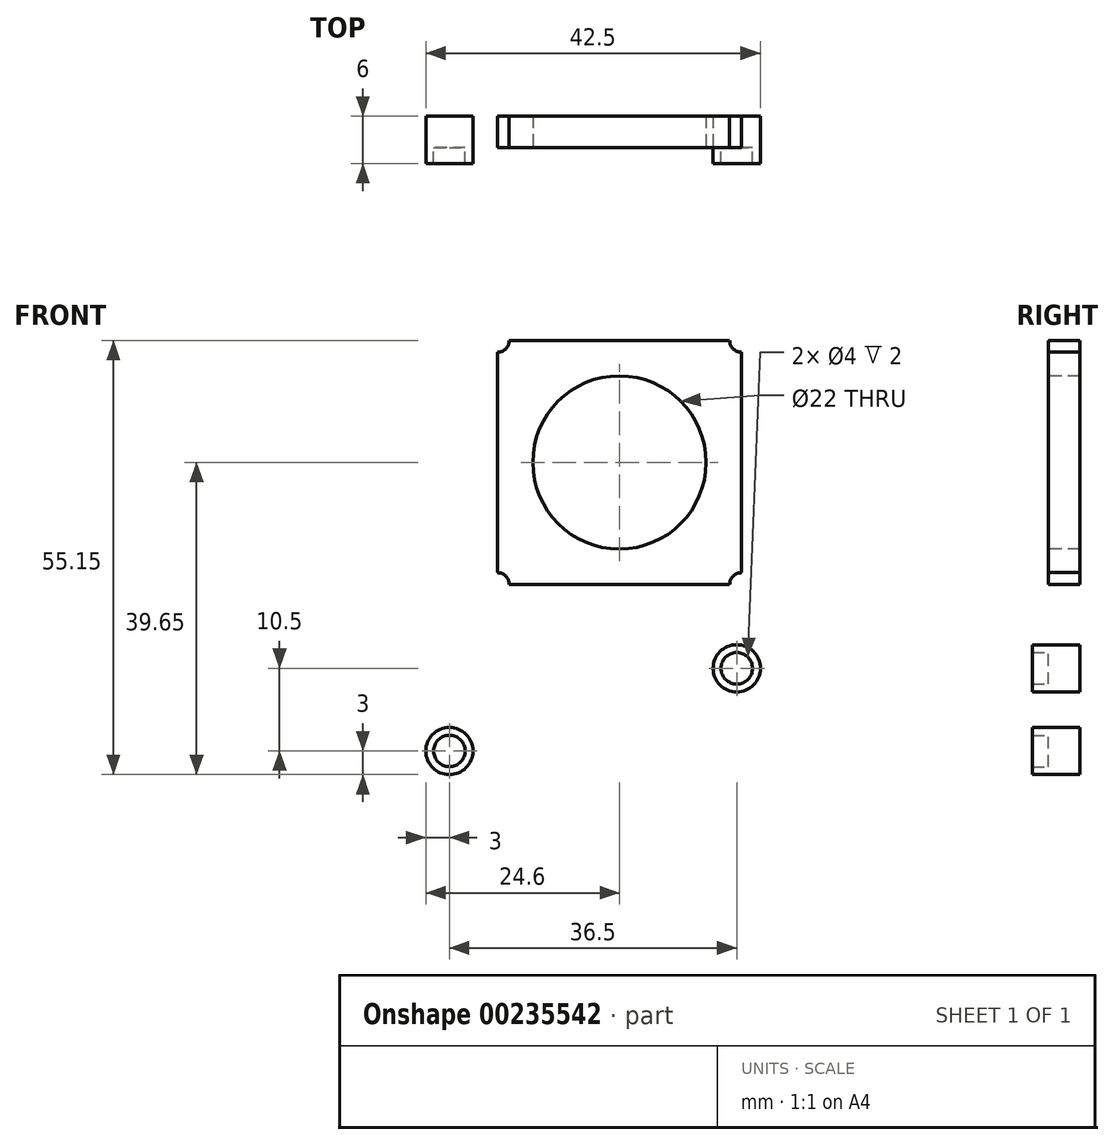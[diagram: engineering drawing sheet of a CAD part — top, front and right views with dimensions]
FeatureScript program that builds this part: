
annotation { "Feature Type Name" : "Feature", "Feature Type Description" : "" }
export const myFeature = defineFeature(function(context is Context, id is Id, definition is map)
    precondition{}
    {
        {
            var Q0;
            Q0=qCreatedBy(makeId("Front.planeOp"),FACE);
            var sketch = newSketch(context, id + "F0", { "sketchPlane" : qUnion([Q0])});
            skLineSegment(sketch, "E0.bottom", {"start": v(21.15, -21.15) * mm, "end": v(-21.15, -21.15) * mm});
            skLineSegment(sketch, "E0.top", {"start": v(21.15, 21.15) * mm, "end": v(-21.15, 21.15) * mm});
            skLineSegment(sketch, "E0.left", {"start": v(21.15, -21.15) * mm, "end": v(21.15, 21.15) * mm});
            skLineSegment(sketch, "E0.right", {"start": v(-21.15, -21.15) * mm, "end": v(-21.15, 21.15) * mm});
            skPoint(sketch, "E0.middle", {"position": v(0, 0) * mm});
            skLineSegment(sketch, "E1.bottom", {"start": v(15.5, -15.5) * mm, "end": v(-15.5, -15.5) * mm});
            skLineSegment(sketch, "E1.top", {"start": v(15.5, 15.5) * mm, "end": v(-15.5, 15.5) * mm});
            skLineSegment(sketch, "E1.left", {"start": v(15.5, -15.5) * mm, "end": v(15.5, 15.5) * mm});
            skLineSegment(sketch, "E1.right", {"start": v(-15.5, -15.5) * mm, "end": v(-15.5, 15.5) * mm});
            skCircle(sketch, "E2", {"center": v(-15.5, 15.5) * mm, "radius": 1.5 * mm});
            skCircle(sketch, "E3", {"center": v(15.5, 15.5) * mm, "radius": 1.5 * mm});
            skCircle(sketch, "E4", {"center": v(-15.5, -15.5) * mm, "radius": 1.5 * mm});
            skCircle(sketch, "E5", {"center": v(15.5, -15.5) * mm, "radius": 1.5 * mm});
            skLineSegment(sketch, "E6.bottom", {"start": v(-21.15, -21.15) * mm, "end": v(21.15, -21.15) * mm});
            skLineSegment(sketch, "E6.top", {"start": v(-21.15, -46.15) * mm, "end": v(21.15, -46.15) * mm});
            skLineSegment(sketch, "E6.right", {"start": v(21.15, -21.15) * mm, "end": v(21.15, -46.15) * mm});
            skCircle(sketch, "E7", {"center": v(0, 0) * mm, "radius": 11 * mm});
            skLineSegment(sketch, "E8.bottom", {"start": v(-21.15, 21.15) * mm, "end": v(21.15, 21.15) * mm});
            skLineSegment(sketch, "E8.top", {"start": v(-21.15, 26.15) * mm, "end": v(21.15, 26.15) * mm});
            skLineSegment(sketch, "E8.left", {"start": v(-21.15, 21.15) * mm, "end": v(-21.15, 26.15) * mm});
            skLineSegment(sketch, "E8.right", {"start": v(21.15, 21.15) * mm, "end": v(21.15, 26.15) * mm});
            skLineSegment(sketch, "E9.bottom", {"start": v(21.15, 26.15) * mm, "end": v(26.15, 26.15) * mm});
            skLineSegment(sketch, "E9.top", {"start": v(21.15, -46.15) * mm, "end": v(26.15, -46.15) * mm});
            skLineSegment(sketch, "E9.left", {"start": v(21.15, 26.15) * mm, "end": v(21.15, -46.15) * mm});
            skLineSegment(sketch, "E9.right", {"start": v(26.15, 26.15) * mm, "end": v(26.15, -46.15) * mm});
            skLineSegment(sketch, "E10.bottom", {"start": v(-21.15, 26.15) * mm, "end": v(-26.15, 26.15) * mm});
            skLineSegment(sketch, "E10.top", {"start": v(-21.15, -46.15) * mm, "end": v(-26.15, -46.15) * mm});
            skLineSegment(sketch, "E10.left", {"start": v(-21.15, 26.15) * mm, "end": v(-21.15, -21.15) * mm});
            skLineSegment(sketch, "E10.right", {"start": v(-26.15, 26.15) * mm, "end": v(-26.15, -46.15) * mm});
            skLineSegment(sketch, "E11.right", {"start": v(-26.15, -41.15) * mm, "end": v(-26.15, -46.15) * mm});
            skLineSegment(sketch, "E12.bottom", {"start": v(-26.15, 26.15) * mm, "end": v(-21.15, 26.15) * mm});
            skLineSegment(sketch, "E12.top", {"start": v(-26.15, 21.15) * mm, "end": v(-21.15, 21.15) * mm});
            skLineSegment(sketch, "E12.left", {"start": v(-26.15, 26.15) * mm, "end": v(-26.15, 21.15) * mm});
            skLineSegment(sketch, "E12.right", {"start": v(-21.15, 26.15) * mm, "end": v(-21.15, 21.15) * mm});
            skLineSegment(sketch, "E13.bottom", {"start": v(26.15, 26.15) * mm, "end": v(21.15, 26.15) * mm});
            skLineSegment(sketch, "E13.top", {"start": v(26.15, 21.15) * mm, "end": v(21.15, 21.15) * mm});
            skLineSegment(sketch, "E13.left", {"start": v(26.15, 26.15) * mm, "end": v(26.15, 21.15) * mm});
            skLineSegment(sketch, "E13.right", {"start": v(21.15, 26.15) * mm, "end": v(21.15, 21.15) * mm});
            skLineSegment(sketch, "E14.bottom", {"start": v(21.15, -21.15) * mm, "end": v(26.15, -21.15) * mm});
            skLineSegment(sketch, "E14.right", {"start": v(26.15, -21.15) * mm, "end": v(26.15, -46.15) * mm});
            skLineSegment(sketch, "E15.bottom", {"start": v(21.15, 26.15) * mm, "end": v(5.15, 26.15) * mm});
            skLineSegment(sketch, "E15.top", {"start": v(21.15, 21.15) * mm, "end": v(5.15, 21.15) * mm});
            skLineSegment(sketch, "E15.right", {"start": v(5.15, 26.15) * mm, "end": v(5.15, 21.15) * mm});
            skLineSegment(sketch, "E16", {"start": v(-21.15, -21.15) * mm, "end": v(-26.15, -21.15) * mm});
            skLineSegment(sketch, "E17", {"start": v(-26.15, -21.15) * mm, "end": v(-21.15, 21.15) * mm});
            skLineSegment(sketch, "E18", {"start": v(15.5, -15.5) * mm, "end": v(14, -15.5) * mm});
            skLineSegment(sketch, "E19", {"start": v(14.9, -13.34) * mm, "end": v(14.9, -14.84) * mm});
            skLineSegment(sketch, "E20", {"start": v(14.9, -14.84) * mm, "end": v(14.9, -26.15) * mm});
            skCircle(sketch, "E21", {"center": v(14.9, -26.15) * mm, "radius": 2 * mm});
            skCircle(sketch, "E22", {"center": v(14.9, -26.15) * mm, "radius": 3 * mm});
            skLineSegment(sketch, "E23", {"start": v(14.9, -26.15) * mm, "end": v(14.9, -36.65) * mm});
            skLineSegment(sketch, "E24", {"start": v(14.9, -36.65) * mm, "end": v(-15.1, -36.65) * mm});
            skLineSegment(sketch, "E25", {"start": v(-15.1, -36.65) * mm, "end": v(-21.6, -36.65) * mm});
            skCircle(sketch, "E26", {"center": v(-21.6, -36.65) * mm, "radius": 3 * mm});
            skCircle(sketch, "E27", {"center": v(-21.6, -36.65) * mm, "radius": 2 * mm});
            skSolve(sketch);
        }
        {
            var Q0;
            Q0=makeQuery(id+"F0.imprint","IMPRINT",FACE,{"disambiguationData":[TD([[makeQuery(id+"F0.imprint","IMPRINT",EDGE,{"derivedFrom":sQuery(id+"F0.wireOp",EDGE,"E6.bottom")}),-1.0]])]});
            var Q1;
            Q1=makeQuery(id+"F0.imprint","IMPRINT",FACE,{"disambiguationData":[TD([[makeQuery(id+"F0.imprint","IMPRINT",EDGE,{"derivedFrom":sQuery(id+"F0.wireOp",EDGE,"E6.bottom")}),1.0]])]});
            var Q2;
            Q2=makeQuery(id+"F0.imprint","IMPRINT",FACE,{"disambiguationData":[TD([[makeQuery(id+"F0.imprint","IMPRINT",EDGE,{"derivedFrom":sQuery(id+"F0.wireOp",EDGE,"E7")}),-1.0]])]});
            var Q3;
            Q3=makeQuery(id+"F0.imprint","IMPRINT",FACE,{"disambiguationData":[TD([[makeQuery(id+"F0.imprint","IMPRINT",EDGE,{"derivedFrom":sQuery(id+"F0.wireOp",EDGE,"E11.bottom")}),1.0]])]});
            var Q4;
            Q4=makeQuery(id+"F0.imprint","IMPRINT",FACE,{"disambiguationData":[TD([[makeQuery(id+"F0.imprint","IMPRINT",EDGE,{"derivedFrom":sQuery(id+"F0.wireOp",EDGE,"E10.left")}),-1.0]])]});
            var Q5;
            Q5=makeQuery(id+"F0.imprint","IMPRINT",FACE,{"disambiguationData":[TD([[makeQuery(id+"F0.imprint","IMPRINT",EDGE,{"derivedFrom":sQuery(id+"F0.wireOp",EDGE,"E21")}),1.0]])]});
            var Q6;
            Q6=makeQuery(id+"F0.imprint","IMPRINT",FACE,{"disambiguationData":[TD([[makeQuery(id+"F0.imprint","IMPRINT",EDGE,{"derivedFrom":sQuery(id+"F0.wireOp",EDGE,"E21")}),-1.0]])]});
            var Q7;
            Q7=makeQuery(id+"F0.imprint","IMPRINT",FACE,{"disambiguationData":[TD([[makeQuery(id+"F0.imprint","IMPRINT",EDGE,{"derivedFrom":sQuery(id+"F0.wireOp",EDGE,"E27")}),1.0]])]});
            var Q8;
            Q8=makeQuery(id+"F0.imprint","IMPRINT",FACE,{"disambiguationData":[TD([[makeQuery(id+"F0.imprint","IMPRINT",EDGE,{"derivedFrom":sQuery(id+"F0.wireOp",EDGE,"E26")}),1.0]])]});
            extrude(context, id + "F1", {"entities" : qUnion([Q0, Q1, Q2, Q3, Q4, Q5, Q6, Q7, Q8]), "oppositeDirection" : true, "depth" : 4 * mm});
        }
        {
            var Q0;
            Q0=makeQuery(id+"F0.imprint","IMPRINT",FACE,{"disambiguationData":[TD([[makeQuery(id+"F0.imprint","IMPRINT",EDGE,{"derivedFrom":sQuery(id+"F0.wireOp",EDGE,"E21")}),-1.0]])]});
            var Q1;
            Q1=makeQuery(id+"F0.imprint","IMPRINT",FACE,{"disambiguationData":[TD([[makeQuery(id+"F0.imprint","IMPRINT",EDGE,{"derivedFrom":sQuery(id+"F0.wireOp",EDGE,"E26")}),1.0]])]});
            extrude(context, id + "F2", {"entities" : qUnion([Q0, Q1]), "operationType" : NewBodyOperationType.ADD, "depth" : 2 * mm});
        }
    });
